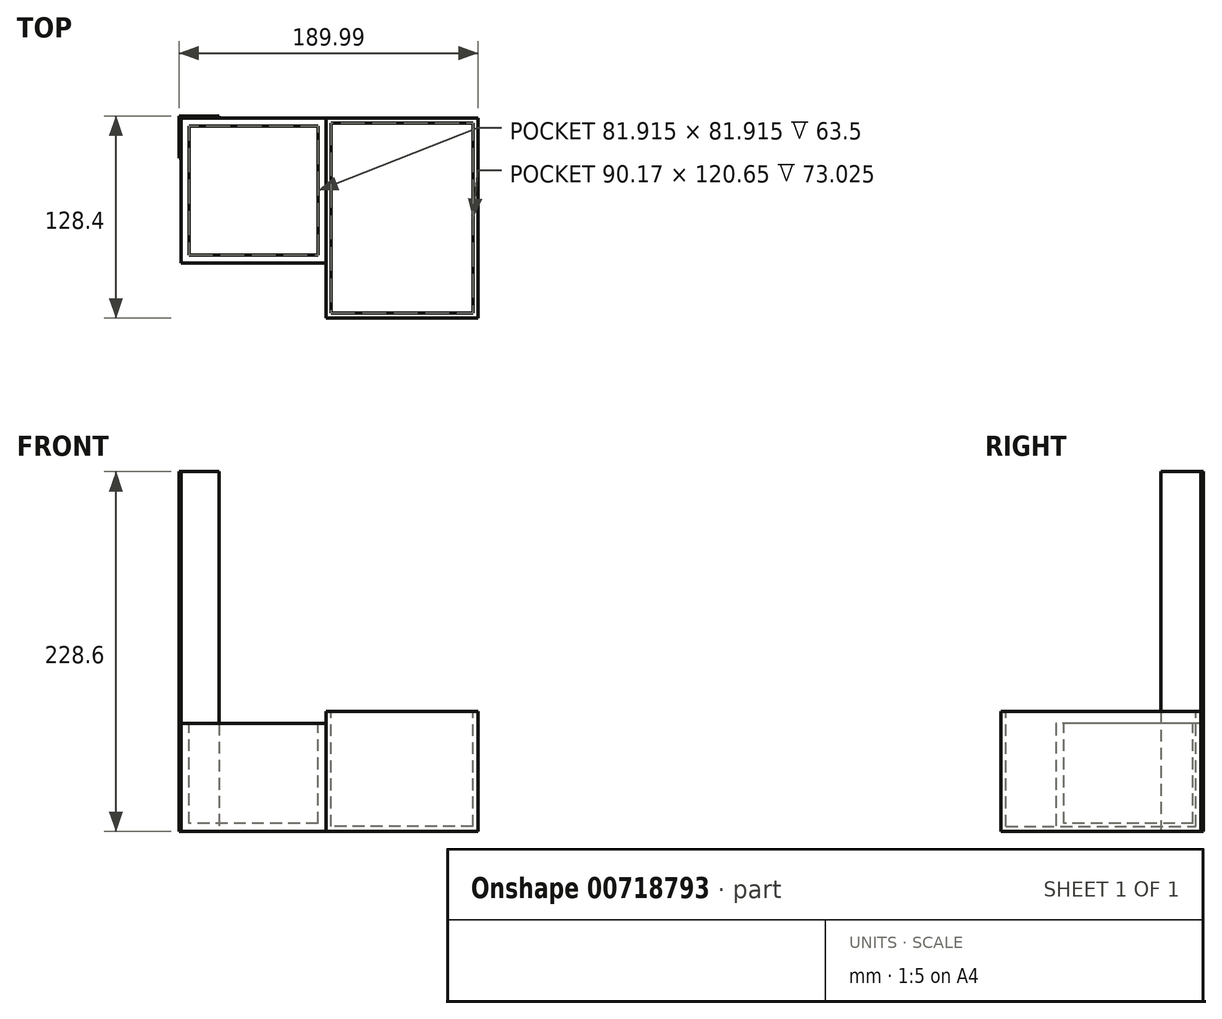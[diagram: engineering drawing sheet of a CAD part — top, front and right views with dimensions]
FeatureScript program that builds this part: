
annotation { "Feature Type Name" : "Feature", "Feature Type Description" : "" }
export const myFeature = defineFeature(function(context is Context, id is Id, definition is map)
    precondition{}
    {
        {
            var Q0;
            Q0=qCreatedBy(makeId("Top.planeOp"),FACE);
            var sketch = newSketch(context, id + "F0", { "sketchPlane" : qUnion([Q0])});
            skLineSegment(sketch, "E0.bottom", {"start": v(48.26, -63.5) * mm, "end": v(-48.26, -63.5) * mm});
            skLineSegment(sketch, "E0.top", {"start": v(48.26, 63.5) * mm, "end": v(-48.26, 63.5) * mm});
            skLineSegment(sketch, "E0.left", {"start": v(48.26, -63.5) * mm, "end": v(48.26, 63.5) * mm});
            skLineSegment(sketch, "E0.right", {"start": v(-48.26, -63.5) * mm, "end": v(-48.26, 63.5) * mm});
            skPoint(sketch, "E0.middle", {"position": v(0, 0) * mm});
            skSolve(sketch);
        }
        {
            var Q0;
            Q0=makeQuery(id+"F0.imprint","IMPRINT",FACE,{"disambiguationData":[TD([[makeQuery(id+"F0.imprint","IMPRINT",EDGE,{"derivedFrom":sQuery(id+"F0.wireOp",EDGE,"E0.bottom")}),-1.0]])]});
            extrude(context, id + "F1", {"entities" : qUnion([Q0]), "depth" : 76.2 * mm, "offsetDistance" : 25.4 * mm});
        }
        {
            var Q0;
            Q0=makeQuery(id+"F1.opExtrude","CAP_FACE",FACE,{"disambiguationData":[OSD([sQuery(id+"F0.wireOp",EDGE,"E0.bottom"),sQuery(id+"F0.wireOp",EDGE,"E0.top"),sQuery(id+"F0.wireOp",EDGE,"E0.left"),sQuery(id+"F0.wireOp",EDGE,"E0.right")])],"isStart":false});
            var sketch = newSketch(context, id + "F2", { "sketchPlane" : qUnion([Q0])});
            skLineSegment(sketch, "E1.bottom", {"start": v(45.08, -60.32) * mm, "end": v(-45.08, -60.33) * mm});
            skLineSegment(sketch, "E1.top", {"start": v(45.08, 60.33) * mm, "end": v(-45.08, 60.32) * mm});
            skLineSegment(sketch, "E1.left", {"start": v(45.08, -60.32) * mm, "end": v(45.08, 60.32) * mm});
            skLineSegment(sketch, "E1.right", {"start": v(-45.08, -60.32) * mm, "end": v(-45.08, 60.32) * mm});
            skPoint(sketch, "E1.middle", {"position": v(0, 0) * mm});
            skSolve(sketch);
        }
        {
            var Q0;
            Q0=makeQuery(id+"F2.imprint","IMPRINT",FACE,{"disambiguationData":[TD([[makeQuery(id+"F2.imprint","IMPRINT",EDGE,{"derivedFrom":sQuery(id+"F2.wireOp",EDGE,"E1.bottom")}),-1.0]])]});
            extrude(context, id + "F3", {"entities" : qUnion([Q0]), "operationType" : NewBodyOperationType.REMOVE, "oppositeDirection" : true, "depth" : 73.02 * mm, "offsetDistance" : 25.4 * mm});
        }
        {
            var Q0;
            Q0=qCreatedBy(makeId("Top.planeOp"),FACE);
            var sketch = newSketch(context, id + "F4", { "sketchPlane" : qUnion([Q0])});
            skLineSegment(sketch, "E2.bottom", {"start": v(-48.26, 63.5) * mm, "end": v(-140.34, 63.5) * mm});
            skLineSegment(sketch, "E2.top", {"start": v(-48.26, -28.58) * mm, "end": v(-140.34, -28.58) * mm});
            skLineSegment(sketch, "E2.left", {"start": v(-48.26, 63.5) * mm, "end": v(-48.26, -28.58) * mm});
            skLineSegment(sketch, "E2.right", {"start": v(-140.34, 63.5) * mm, "end": v(-140.34, -28.58) * mm});
            skSolve(sketch);
        }
        {
            var Q0;
            Q0 = qSketchRegion(id + "F4", true);
            extrude(context, id + "F5", {"entities" : qUnion([Q0]), "depth" : 68.58 * mm, "offsetDistance" : 25.4 * mm});
        }
        {
            var Q0;
            Q0=makeQuery(id+"F5.opExtrude","CAP_FACE",FACE,{"disambiguationData":[OSD([sQuery(id+"F4.wireOp",EDGE,"E2.bottom"),sQuery(id+"F4.wireOp",EDGE,"E2.top"),sQuery(id+"F4.wireOp",EDGE,"E2.left"),sQuery(id+"F4.wireOp",EDGE,"E2.right")])],"isStart":false});
            var sketch = newSketch(context, id + "F6", { "sketchPlane" : qUnion([Q0])});
            skLineSegment(sketch, "E3.bottom", {"start": v(-53.34, 58.42) * mm, "end": v(-135.26, 58.42) * mm});
            skLineSegment(sketch, "E3.top", {"start": v(-53.34, -23.5) * mm, "end": v(-135.26, -23.5) * mm});
            skLineSegment(sketch, "E3.left", {"start": v(-53.34, 58.42) * mm, "end": v(-53.34, -23.5) * mm});
            skLineSegment(sketch, "E3.right", {"start": v(-135.26, 58.42) * mm, "end": v(-135.26, -23.5) * mm});
            skSolve(sketch);
        }
        {
            var Q0;
            Q0 = qSketchRegion(id + "F6", true);
            extrude(context, id + "F7", {"entities" : qUnion([Q0]), "operationType" : NewBodyOperationType.REMOVE, "oppositeDirection" : true, "depth" : 63.5 * mm, "offsetDistance" : 25.4 * mm});
        }
        {
            var Q0;
            Q0=qCreatedBy(makeId("Top.planeOp"),FACE);
            var sketch = newSketch(context, id + "F8", { "sketchPlane" : qUnion([Q0])});
            skLineSegment(sketch, "E4.bottom", {"start": v(-140.34, 63.5) * mm, "end": v(-141.73, 63.5) * mm});
            skLineSegment(sketch, "E4.top", {"start": v(-140.34, 38.1) * mm, "end": v(-141.73, 38.1) * mm});
            skLineSegment(sketch, "E4.left", {"start": v(-140.34, 63.5) * mm, "end": v(-140.34, 38.1) * mm});
            skLineSegment(sketch, "E4.right", {"start": v(-141.73, 63.5) * mm, "end": v(-141.73, 38.1) * mm});
            skLineSegment(sketch, "E5.bottom", {"start": v(-141.73, 63.5) * mm, "end": v(-116.33, 63.5) * mm});
            skLineSegment(sketch, "E5.top", {"start": v(-141.73, 64.9) * mm, "end": v(-116.33, 64.9) * mm});
            skLineSegment(sketch, "E5.left", {"start": v(-141.73, 63.5) * mm, "end": v(-141.73, 64.9) * mm});
            skLineSegment(sketch, "E5.right", {"start": v(-116.33, 63.5) * mm, "end": v(-116.33, 64.9) * mm});
            skSolve(sketch);
        }
        {
            var Q0;
            {var subQ0=makeQuery(id+"F8.imprint","IMPRINT",EDGE,{"derivedFrom":sQuery(id+"F8.wireOp",EDGE,"E4.bottom")});Q0=qUnion([makeQuery(id+"F8.imprint","IMPRINT",FACE,{"disambiguationData":[TD([[subQ0,1.0]])]}),makeQuery(id+"F8.imprint","IMPRINT",FACE,{"disambiguationData":[TD([[subQ0,-1.0]])]})]);}
            extrude(context, id + "F9", {"entities" : qUnion([Q0]), "depth" : 228.6 * mm, "offsetDistance" : 25.4 * mm});
        }
    });
